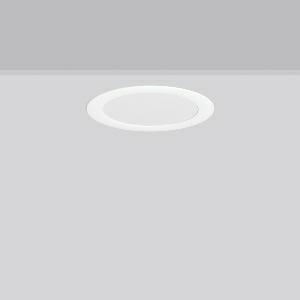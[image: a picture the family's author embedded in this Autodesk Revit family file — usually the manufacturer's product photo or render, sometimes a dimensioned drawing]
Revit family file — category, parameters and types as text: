
# Revit family: toledo_flat_round_e_672224_002_1_a579
name_source: partatom
category: Lighting Fixtures
units: mm (PartAtom-declared; Revit-internal decimal feet)

## family parameters
Cut with Voids When Loaded = No
Host = Face
Light Source = No
Part Type = Normal
Room Calculation Point = No
Round Connector Dimension = Use Diameter
Shared = No

## types (1)
- TOLEDO FLAT round E (1 x LED Modul 840, 1800 lm, 4000)
    Apparent Load = 17 VA
    CIE Flux Codes = 48 79 96 100 100
    Color Rendering = 80
    Color Temperature = 4000
    Default Elevation = 1800 mm  [stored 5.90551 ft]
    Description = Series: TOLEDO FLAT round
Ultra thin recessed downlight. For escape route illumination. Housing: die-cast aluminium, powder-coated. Lightguide and diffuser made of non-yellowing plastic (PMMA). Diffuser opal matt plastic. Ceiling installation with spring system. Including separate LED converter with connecting cable 250 mm. Self-contained system with automatic self-test. External driver with simple plug-in locking system. 
Colour: white
Diameter: 255 mm
Height: 3 mm
Cut-out diameter: 234 mm
Recess height: 100 mm
Luminaire: recess height: 60-80 mm
Weight: 1.76 kg
Operating mode: maintained power mode
Duration time: 3 h
Lamp: LED
Socket: without socket
Colour temperature: 4000K
Colour rendering index (CRI): 80
System power: 17 W
Rated luminous flux: 1800 lm
Luminous flux, emergency: 460 lm
System power, emergency: -
Control gear: Regulated power supply
Protection class: I
Type of protection: IP 54
    Height = 0 mm  [stored 0 ft]
    Lamp = 1 x LED Modul 840
    Lamp Light Flux = 1800 lm
    Lamp count = 1
    Length = 255 mm
    Lifetime = 50000 h
    Luminous efficacy = 106 lm/W
    Manufacturer = RZB
    ModVariant = No
    Model = 672224.002.1
    Mounting Place = Ceiling
    Mounting Type = Recessed
    Number of Poles = 1
    OnlyDefault = Yes
    Power Factor = 1
    Product Name = TOLEDO FLAT round E
    Product group = Recessed downlights
    ProductGroupID = 402
    Protection Class = Protection class I
    Protection Degree = IP 40
    RLX_Detail_Level = 1
    RLX_Emergency_Light_Flux = 460 lm
    RLX_Emergency_Type = 3
    RLX_Emergency_Type_DB = Yes
    RlxData = <blob elided: 30441 chars, md5=a89282ea>
    Socket = socket
    Standby Power = 0 W
    System Light Flux = 1800 lm
    System Power = 17 W
    Type Comments = Product without accessories
    Type Image = 901453.002.jpg
    URL = http://relux.com
    VarID = ---
    Voltage = 0 V
    Weight = 0.00 kg
    Width = 0 mm  [stored 0 ft]

note: [stored X ft] marks values corroborated as IEEE doubles in the binary element streams (Revit-internal decimal feet)

## geometry (parser evidence)
native form markers: Blend x4, Sweep x13
no freeform markers — native parametric forms only
